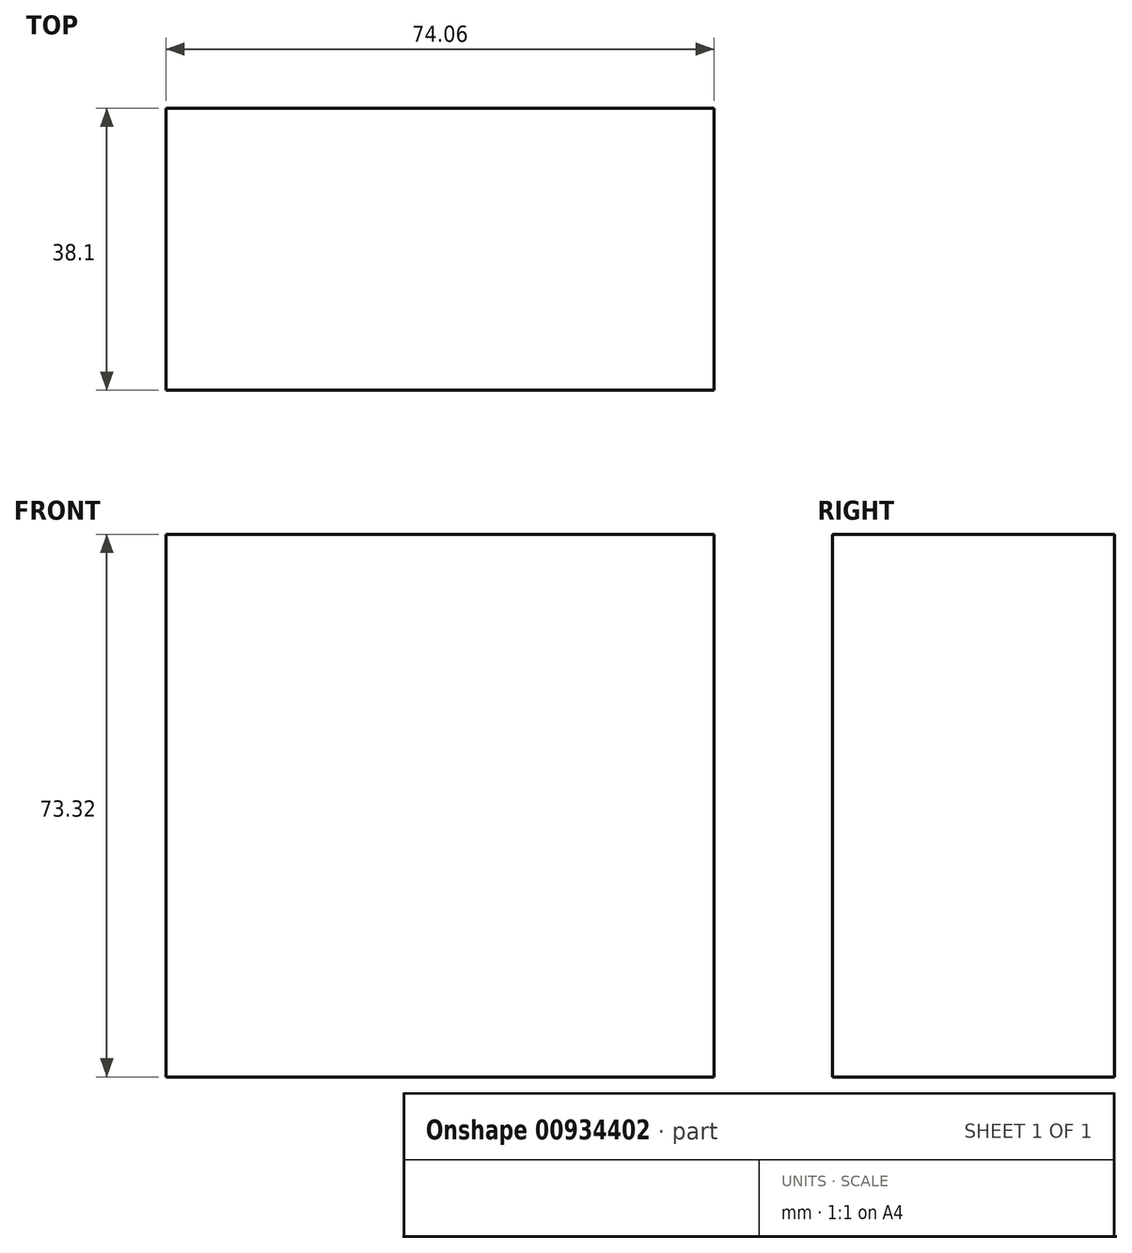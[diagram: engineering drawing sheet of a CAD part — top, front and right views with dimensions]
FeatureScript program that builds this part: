
annotation { "Feature Type Name" : "Feature", "Feature Type Description" : "" }
export const myFeature = defineFeature(function(context is Context, id is Id, definition is map)
    precondition{}
    {
        {
            var Q0;
            Q0=qCreatedBy(makeId("Front.planeOp"),FACE);
            var sketch = newSketch(context, id + "F0", { "sketchPlane" : qUnion([Q0])});
            skLineSegment(sketch, "E0.bottom", {"start": v(0, 0) * mm, "end": v(-74.06, 0) * mm});
            skLineSegment(sketch, "E0.top", {"start": v(0, 73.32) * mm, "end": v(-74.06, 73.32) * mm});
            skLineSegment(sketch, "E0.left", {"start": v(0, 0) * mm, "end": v(0, 73.32) * mm});
            skLineSegment(sketch, "E0.right", {"start": v(-74.06, 0) * mm, "end": v(-74.06, 73.32) * mm});
            skSolve(sketch);
        }
        {
            var Q0;
            Q0=makeQuery(id+"F0.imprint","IMPRINT",FACE,{"disambiguationData":[TD([[makeQuery(id+"F0.imprint","IMPRINT",EDGE,{"derivedFrom":sQuery(id+"F0.wireOp",EDGE,"E0.bottom")}),-1.0]])]});
            extrude(context, id + "F1", {"entities" : qUnion([Q0]), "depth" : 38.1 * mm, "offsetDistance" : 25.4 * mm});
        }
    });
